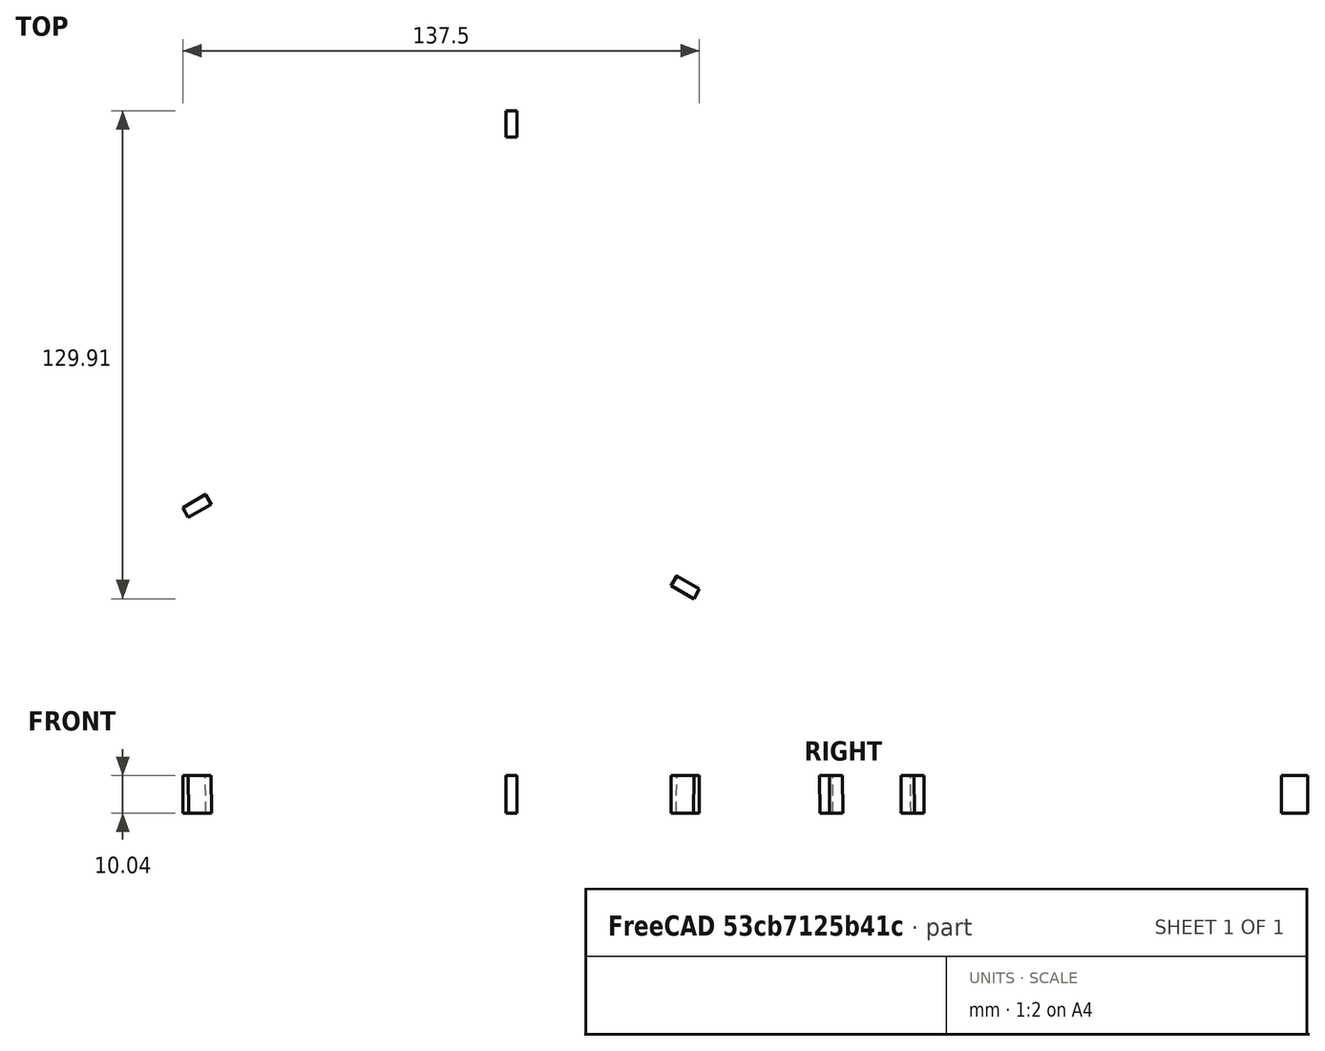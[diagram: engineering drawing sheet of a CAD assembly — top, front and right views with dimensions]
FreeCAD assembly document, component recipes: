
FREECAD ASSEMBLY — COMPONENT RECIPES ("deltarobot-example")

This assembly document has 17 components, labeled P0..P16 below (a component is one placed body or linked part). 17 of them carry a construction recipe — the FreeCAD feature program that regenerates the part from scratch, quoted from this document or its linked companion documents; the rest are supplied as boundary geometry only. No exploded tour is included for this assembly.
COMPONENT P0 — recipe-attached ("arm", a linked part whose construction recipe lives in a companion FreeCAD document of the same project; that document's serialized recipe follows).
Construction recipe (the companion document, serialized — sketch geometry with constraints, then the solid features built on it; lengths are millimeters unless a unit is written):

FCSTD DOCUMENT  (FreeCAD 2024.1R35694 (Git))
Label: arm
License: All rights reserved
LicenseURL: http://en.wikipedia.org/wiki/All_rights_reserved
objects: Sketcher::SketchObject×11, PartDesign::Pad×6, PartDesign::Plane×2, PartDesign::Revolution×2, PartDesign::Mirrored×2, PartDesign::Body×2, PartDesign::Pocket×2, PartDesign::Chamfer×1, PartDesign::Hole×1, PartDesign::Fillet×1, App::Part×1
note: 43 computed .brp shape members not serialized (recipe doc carries the construction recipe); baked Part::Feature solids carry a one-line shape summary decoded from their .brp

FEATURE [PartDesign::Plane] DatumPlane002  label="midplane001"
  AttachmentOffset = pos=(0,0,7) rot=(0,0,1;0rad)
  Length = 60
  MapMode = 5
  Placement = pos=(0,-7,1.6e-15) rot=(1,0,0;1.5708rad)
  ResizeMode = 0
  Support = -> [XZ_Plane002]
  Width = 60
FEATURE [Sketcher::SketchObject] Sketch008
  FullyConstrained = true
  MapMode = 5
  Placement = pos=(0,0,0) rot=(1,0,0;1.5708rad)
  Support = -> [XZ_Plane002]
  sketch-geometry (5):
    g0: Circle CenterX=0 CenterY=0 CenterZ=0 NormalX=0 NormalY=0 NormalZ=1 AngleXU=0 Radius=2.5
    g1: ArcOfCircle CenterX=0 CenterY=0 CenterZ=0 NormalX=0 NormalY=0 NormalZ=1 AngleXU=0 Radius=6 StartAngle=3.14159 EndAngle=6.28319
    g2: LineSegment StartX=-6 StartY=-1.9e-15 StartZ=0 EndX=-6 EndY=50 EndZ=0
    g3: LineSegment StartX=6 StartY=-1.5e-15 StartZ=0 EndX=6 EndY=50 EndZ=0
    g4: LineSegment StartX=-6 StartY=50 StartZ=0 EndX=6 EndY=50 EndZ=0
  constraints (12):
    c: Coincident(g0,g-1)
    c: Tangent(g1,g2) = 1.5708
    c: Tangent(g1,g3) = -1.5708
    c: Vertical(g3)
    c: Diameter(g0) = 5
    c: Distance(g1,g1) = 12
    c: PointOnObject(g1,g-1)
    c: Coincident(g4,g2)
    c: Coincident(g4,g3)
    c: DistanceY(g3,g3) = 50
    c: Vertical(g2)
    c: Symmetric(g2,g3,g-2)
FEATURE [PartDesign::Pad] Pad003
  Direction = (0,-1,2e-16)
  Length = 8
  Length2 = 10
  Midplane = true
  Placement = pos=(0,0,0) rot=(1,0,0;1.5708rad)
  Profile = -> Sketch008
  ReferenceAxis = -> Sketch008 [N_Axis]
  Type = 0
FEATURE [Sketcher::SketchObject] Sketch009
  FullyConstrained = true
  MapMode = 5
  Placement = pos=(0,0,0) rot=(1,0,0;1.5708rad)
  Support = -> [XZ_Plane002]
  sketch-geometry (2):
    g0: Circle CenterX=0 CenterY=0 CenterZ=0 NormalX=0 NormalY=0 NormalZ=1 AngleXU=0 Radius=2.5
    g1: Circle CenterX=0 CenterY=0 CenterZ=0 NormalX=0 NormalY=0 NormalZ=1 AngleXU=0 Radius=6
  constraints (4):
    c: Coincident(g0,g-1)
    c: Coincident(g1,g0)
    c: Diameter(g0) = 5
    c: Diameter(g1) = 12
FEATURE [PartDesign::Pad] Pad004
  BaseFeature = -> Pad003
  Direction = (0,-1,2e-16)
  Length = 10
  Length2 = 10
  Placement = pos=(0,0,0) rot=(1,0,0;1.5708rad)
  Profile = -> Sketch009
  ReferenceAxis = -> Sketch009 [N_Axis]
  Refine = true
  Type = 0
FEATURE [Sketcher::SketchObject] Sketch010
  ExternalGeometry = -> [Pad004]
  FullyConstrained = true
  MapMode = 5
  Placement = pos=(0,-7,1.6e-15) rot=(1,0,0;1.5708rad)
  Support = -> [DatumPlane002]
  sketch-geometry (4):
    g0: LineSegment StartX=-6 StartY=50 StartZ=0 EndX=6 EndY=50 EndZ=0
    g1: LineSegment StartX=6 StartY=50 StartZ=0 EndX=6 EndY=56 EndZ=0
    g2: LineSegment StartX=6 StartY=56 StartZ=0 EndX=-6 EndY=56 EndZ=0
    g3: LineSegment StartX=-6 StartY=56 StartZ=0 EndX=-6 EndY=50 EndZ=0
  constraints (10):
    c: Coincident(g0,g1)
    c: Coincident(g1,g2)
    c: Coincident(g2,g3)
    c: Coincident(g3,g0)
    c: Horizontal(g2)
    c: Vertical(g1)
    c: Vertical(g3)
    c: Coincident(g0,g-3)
    c: Coincident(g0,g-3)
    c: DistanceY(g1,g1) = 6
FEATURE [PartDesign::Pad] Pad005
  BaseFeature = -> Pad004
  Direction = (0,-1,2e-16)
  Length = 36
  Length2 = 10
  Midplane = true
  Placement = pos=(0,0,0) rot=(1,0,0;1.5708rad)
  Profile = -> Sketch010
  ReferenceAxis = -> Sketch010 [N_Axis]
  Refine = true
  Type = 0
FEATURE [Sketcher::SketchObject] Sketch011
  ExternalGeometry = -> [Pad005,DatumPlane002]
  FullyConstrained = true
  MapMode = 5
  Placement = pos=(0,0,0) rot=(0.57735,0.57735,0.57735;2.0944rad)
  Support = -> [YZ_Plane002]
  sketch-geometry (4):
    g0: LineSegment StartX=-37 StartY=53 StartZ=0 EndX=-25 EndY=53 EndZ=0
    g1: ArcOfCircle CenterX=-32 CenterY=53 CenterZ=0 NormalX=0 NormalY=0 NormalZ=1 AngleXU=0 Radius=5 StartAngle=0.643501 EndAngle=3.14159
    g2: LineSegment StartX=-28 StartY=56 StartZ=0 EndX=-25 EndY=56 EndZ=0
    g3: LineSegment StartX=-25 StartY=56 StartZ=0 EndX=-25 EndY=53 EndZ=0
  constraints (12):
    c: Symmetric(g-3,g-3,g0)
    c: PointOnObject(g1,g0)
    c: Coincident(g1,g0)
    c: PointOnObject(g0,g-3)
    c: Radius(g1) = 5
    c: Distance(g1,g-4) = 25
    c: Coincident(g1,g2)
    c: PointOnObject(g2,g-3)
    c: Horizontal(g2)
    c: Coincident(g2,g3)
    c: Coincident(g3,g0)
    c: DistanceY(g0,g2) = 3
FEATURE [PartDesign::Revolution] Revolution
  Angle = 360
  Angle2 = 60
  Axis = (0,1,0)
  Base = (0,-37,53)
  BaseFeature = -> Pad005
  Placement = pos=(0,0,0) rot=(1,0,0;1.5708rad)
  Profile = -> Sketch011
  ReferenceAxis = -> Sketch011 [Edge1]
  Refine = true
  Type = 0
FEATURE [PartDesign::Mirrored] Mirrored002
  BaseFeature = -> Revolution
  MirrorPlane = -> DatumPlane002
  Originals = -> [Revolution]
  Placement = pos=(0,0,0) rot=(1,0,0;1.5708rad)
  Refine = true
FEATURE [PartDesign::Body] Body001  label="arm-skeleton"
  Group = -> [Sketch008,Pad003,Sketch009,Pad004,DatumPlane002,Sketch010,Pad005,Sketch011,Revolution,Mirrored002]
  Origin = -> Origin002
  Tip = -> Mirrored002
FEATURE [PartDesign::Plane] DatumPlane003  label="midplane002"
  AttachmentOffset = pos=(0,0,7) rot=(0,0,1;0rad)
  Length = 60
  MapMode = 5
  Placement = pos=(0,-7,1.6e-15) rot=(1,0,0;1.5708rad)
  ResizeMode = 0
  Support = -> [XZ_Plane002]
  Width = 60
FEATURE [Sketcher::SketchObject] Sketch012
  FullyConstrained = true
  MapMode = 5
  Placement = pos=(0,0,0) rot=(1,0,0;1.5708rad)
  Support = -> [XZ_Plane003]
  sketch-geometry (5):
    g0: Circle CenterX=0 CenterY=0 CenterZ=0 NormalX=0 NormalY=0 NormalZ=1 AngleXU=0 Radius=2.5
    g1: ArcOfCircle CenterX=0 CenterY=0 CenterZ=0 NormalX=0 NormalY=0 NormalZ=1 AngleXU=0 Radius=6 StartAngle=3.14159 EndAngle=6.28319
    g2: LineSegment StartX=-6 StartY=-1.9e-15 StartZ=0 EndX=-6 EndY=50 EndZ=0
    g3: LineSegment StartX=6 StartY=-1.5e-15 StartZ=0 EndX=6 EndY=50 EndZ=0
    g4: LineSegment StartX=-6 StartY=50 StartZ=0 EndX=6 EndY=50 EndZ=0
  constraints (12):
    c: Coincident(g0,g-1)
    c: Tangent(g1,g2) = 1.5708
    c: Tangent(g1,g3) = -1.5708
    c: Vertical(g3)
    c: Diameter(g0) = 5
    c: Distance(g1,g1) = 12
    c: PointOnObject(g1,g-1)
    c: Coincident(g4,g2)
    c: Coincident(g4,g3)
    c: DistanceY(g3,g3) = 50
    c: Vertical(g2)
    c: Symmetric(g2,g3,g-2)
FEATURE [PartDesign::Pad] Pad006
  Direction = (0,-1,2e-16)
  Length = 8
  Length2 = 10
  Midplane = true
  Placement = pos=(0,0,0) rot=(1,0,0;1.5708rad)
  Profile = -> Sketch012
  ReferenceAxis = -> Sketch012 [N_Axis]
  Type = 0
FEATURE [Sketcher::SketchObject] Sketch013
  FullyConstrained = true
  MapMode = 5
  Placement = pos=(0,0,0) rot=(1,0,0;1.5708rad)
  Support = -> [XZ_Plane003]
  sketch-geometry (2):
    g0: Circle CenterX=0 CenterY=0 CenterZ=0 NormalX=0 NormalY=0 NormalZ=1 AngleXU=0 Radius=2.5
    g1: Circle CenterX=0 CenterY=0 CenterZ=0 NormalX=0 NormalY=0 NormalZ=1 AngleXU=0 Radius=6
  constraints (4):
    c: Coincident(g0,g-1)
    c: Coincident(g1,g0)
    c: Diameter(g0) = 5
    c: Diameter(g1) = 12
FEATURE [PartDesign::Pad] Pad007
  BaseFeature = -> Pad006
  Direction = (0,-1,2e-16)
  Length = 10
  Length2 = 10
  Placement = pos=(0,0,0) rot=(1,0,0;1.5708rad)
  Profile = -> Sketch013
  ReferenceAxis = -> Sketch013 [N_Axis]
  Refine = true
  Type = 0
FEATURE [Sketcher::SketchObject] Sketch014
  ExternalGeometry = -> [Pad007]
  FullyConstrained = true
  MapMode = 5
  Placement = pos=(0,-7,1.6e-15) rot=(1,0,0;1.5708rad)
  Support = -> [DatumPlane003]
  sketch-geometry (4):
    g0: LineSegment StartX=-6 StartY=50 StartZ=0 EndX=6 EndY=50 EndZ=0
    g1: LineSegment StartX=6 StartY=50 StartZ=0 EndX=6 EndY=56 EndZ=0
    g2: LineSegment StartX=6 StartY=56 StartZ=0 EndX=-6 EndY=56 EndZ=0
    g3: LineSegment StartX=-6 StartY=56 StartZ=0 EndX=-6 EndY=50 EndZ=0
  constraints (10):
    c: Coincident(g0,g1)
    c: Coincident(g1,g2)
    c: Coincident(g2,g3)
    c: Coincident(g3,g0)
    c: Horizontal(g2)
    c: Vertical(g1)
    c: Vertical(g3)
    c: Coincident(g0,g-3)
    c: Coincident(g0,g-3)
    c: DistanceY(g1,g1) = 6
FEATURE [PartDesign::Pad] Pad008
  BaseFeature = -> Pad007
  Direction = (0,-1,2e-16)
  Length = 36
  Length2 = 10
  Midplane = true
  Placement = pos=(0,0,0) rot=(1,0,0;1.5708rad)
  Profile = -> Sketch014
  ReferenceAxis = -> Sketch014 [N_Axis]
  Refine = true
  Type = 0
FEATURE [Sketcher::SketchObject] Sketch015
  ExternalGeometry = -> [Pad008,DatumPlane003]
  FullyConstrained = true
  MapMode = 5
  Placement = pos=(0,0,0) rot=(0.57735,0.57735,0.57735;2.0944rad)
  Support = -> [YZ_Plane003]
  sketch-geometry (4):
    g0: LineSegment StartX=-36.9 StartY=53 StartZ=0 EndX=-25 EndY=53 EndZ=0
    g1: ArcOfCircle CenterX=-32 CenterY=53 CenterZ=0 NormalX=0 NormalY=0 NormalZ=1 AngleXU=0 Radius=4.9 StartAngle=0.658897 EndAngle=3.14159
    g2: LineSegment StartX=-28.1257 StartY=56 StartZ=0 EndX=-25 EndY=56 EndZ=0
    g3: LineSegment StartX=-25 StartY=56 StartZ=0 EndX=-25 EndY=53 EndZ=0
  constraints (12):
    c: Symmetric(g-3,g-3,g0)
    c: PointOnObject(g1,g0)
    c: Coincident(g1,g0)
    c: PointOnObject(g0,g-3)
    c: Radius(g1) = 4.9
    c: Distance(g1,g-4) = 25
    c: Coincident(g1,g2)
    c: PointOnObject(g2,g-3)
    c: Horizontal(g2)
    c: Coincident(g2,g3)
    c: Coincident(g3,g0)
    c: DistanceY(g0,g2) = 3
FEATURE [PartDesign::Revolution] Revolution001
  Angle = 360
  Angle2 = 60
  Axis = (0,1,0)
  Base = (0,-36.9,53)
  BaseFeature = -> Pad008
  Placement = pos=(0,0,0) rot=(1,0,0;1.5708rad)
  Profile = -> Sketch015
  ReferenceAxis = -> Sketch015 [Edge1]
  Refine = true
  Type = 0
FEATURE [PartDesign::Mirrored] Mirrored003
  BaseFeature = -> Revolution001
  MirrorPlane = -> DatumPlane003
  Originals = -> [Revolution001]
  Placement = pos=(0,0,0) rot=(1,0,0;1.5708rad)
  Refine = true
FEATURE [PartDesign::Chamfer] Chamfer
  Angle = 45
  Base = -> Mirrored003 [Edge12,Edge10,Edge17,Edge21]
  BaseFeature = -> Mirrored003
  ChamferType = 0
  FlipDirection = false
  Placement = pos=(0,0,0) rot=(1,0,0;1.5708rad)
  Refine = true
  Size = 2
  Size2 = 1
  SupportTransform = false
  UseAllEdges = false
FEATURE [Sketcher::SketchObject] Sketch
  FullyConstrained = true
  MapMode = 5
  Placement = pos=(0,0,0) rot=(1,0,0;1.5708rad)
  Support = -> [XZ_Plane003]
  sketch-geometry (4):
    g0: LineSegment StartX=0.5 StartY=0 StartZ=0 EndX=0.5 EndY=10 EndZ=0
    g1: LineSegment StartX=0.5 StartY=10 StartZ=0 EndX=-0.5 EndY=10 EndZ=0
    g2: LineSegment StartX=-0.5 StartY=10 StartZ=0 EndX=-0.5 EndY=0 EndZ=0
    g3: LineSegment StartX=-0.5 StartY=0 StartZ=0 EndX=0.5 EndY=0 EndZ=0
  constraints (11):
    c: Coincident(g0,g1)
    c: Coincident(g1,g2)
    c: Coincident(g2,g3)
    c: Coincident(g3,g0)
    c: Vertical(g0)
    c: Vertical(g2)
    c: Horizontal(g1)
    c: Horizontal(g3)
    c: Symmetric(g2,g0,g-1)
    c: Distance(g1,g1) = 1
    c: DistanceY(g0,g0) = 10
FEATURE [PartDesign::Pocket] Pocket
  BaseFeature = -> Chamfer
  Direction = (0,1,-2e-16)
  Length = 5
  Length2 = 5
  Midplane = true
  Placement = pos=(0,0,0) rot=(1,0,0;1.5708rad)
  Profile = -> Sketch
  ReferenceAxis = -> Sketch [N_Axis]
  Refine = true
  Type = 1
FEATURE [Sketcher::SketchObject] Sketch016
  FullyConstrained = true
  MapMode = 5
  Placement = pos=(6,0,0) rot=(0.707107,0,0.707107;3.14159rad)
  Support = -> [Pocket]
  sketch-geometry (1):
    g0: Circle CenterX=5 CenterY=0 CenterZ=0 NormalX=0 NormalY=0 NormalZ=1 AngleXU=0 Radius=1.5
  constraints (3):
    c: PointOnObject(g0,g-1)
    c: Diameter(g0) = 3
    c: DistanceX(g-1,g0) = 5
FEATURE [PartDesign::Hole] Hole
  BaseFeature = -> Pocket
  CustomThreadClearance = 0
  Depth = 178.805
  DepthType = 1
  Diameter = 3.4
  DrillForDepth = false
  DrillPoint = 1
  DrillPointAngle = 118
  HoleCutCountersinkAngle = 90
  HoleCutCustomValues = false
  HoleCutDepth = 0
  HoleCutDiameter = 6.1
  HoleCutType = 0
  ModelThread = false
  Placement = pos=(0,0,0) rot=(1,0,0;1.5708rad)
  Profile = -> Sketch016
  Refine = true
  Tapered = false
  TaperedAngle = 90
  ThreadClass = 0
  ThreadDepth = 178.805
  ThreadDepthType = 0
  ThreadDirection = 0
  ThreadFit = 0
  ThreadSize = 9
  ThreadType = 1
  Threaded = false
  UseCustomThreadClearance = false
FEATURE [Sketcher::SketchObject] Sketch017
  ExternalGeometry = -> [Hole]
  FullyConstrained = true
  MapMode = 5
  Placement = pos=(-6,0,0) rot=(0.707107,0,-0.707107;3.14159rad)
  Support = -> [Hole]
  sketch-geometry (7):
    g0: LineSegment StartX=-1.5359 StartY=-4e-16 StartZ=0 EndX=-3.26795 EndY=3 EndZ=0
    g1: LineSegment StartX=-3.26795 StartY=3 StartZ=0 EndX=-6.73205 EndY=3 EndZ=0
    g2: LineSegment StartX=-6.73205 StartY=3 StartZ=0 EndX=-8.4641 EndY=-9e-16 EndZ=0
    g3: LineSegment StartX=-8.4641 StartY=-9e-16 StartZ=0 EndX=-6.73205 EndY=-3 EndZ=0
    g4: LineSegment StartX=-6.73205 StartY=-3 StartZ=0 EndX=-3.26795 EndY=-3 EndZ=0
    g5: LineSegment StartX=-3.26795 StartY=-3 StartZ=0 EndX=-1.5359 EndY=-4e-16 EndZ=0
    g6: Circle CenterX=-5 CenterY=-6e-16 CenterZ=0 NormalX=0 NormalY=0 NormalZ=1 AngleXU=0 Radius=3.4641
  constraints (16):
    c: Coincident(g0,g1)
    c: Coincident(g1,g2)
    c: Coincident(g2,g3)
    c: Coincident(g3,g4)
    c: Coincident(g4,g5)
    c: Coincident(g5,g0)
    c: Equal(g0, g1-g5) x5
    c: PointOnObject(g0,g6)
    c: PointOnObject(g1,g6)
    c: PointOnObject(g2,g6)
    c: PointOnObject(g3,g6)
    c: PointOnObject(g4,g6)
    c: PointOnObject(g5,g6)
    c: Coincident(g6,g-3)
    c: DistanceY(g4,g0) = 6
    c: Horizontal(g1)
FEATURE [PartDesign::Pocket] Pocket001
  BaseFeature = -> Hole
  Direction = (1,0,2e-16)
  Length = 3
  Length2 = 5
  Placement = pos=(0,0,0) rot=(1,0,0;1.5708rad)
  Profile = -> Sketch017
  ReferenceAxis = -> Sketch017 [N_Axis]
  Refine = true
  Type = 0
FEATURE [PartDesign::Fillet] Fillet
  Base = -> Pocket001 [Edge3,Edge46]
  BaseFeature = -> Pocket001
  Placement = pos=(0,0,0) rot=(1,0,0;1.5708rad)
  Radius = 2
  Refine = true
  SupportTransform = false
  UseAllEdges = false
FEATURE [PartDesign::Body] Body002  label="arm0"
  Group = -> [Sketch012,Pad006,Sketch013,Pad007,DatumPlane003,Sketch014,Pad008,Sketch015,Revolution001,Mirrored003,Chamfer,Sketch,Pocket,Sketch016,Hole,Sketch017,Pocket001,Fillet]
  Origin = -> Origin003
  Tip = -> Fillet
FEATURE [App::Part] Part  label="arm"
  Group = -> [Body001,Body002]
  Origin = -> Origin
COMPONENT P1 — same part as P0; its construction recipe is shown at P0.
COMPONENT P2 — same part as P0; its construction recipe is shown at P0.
COMPONENT P3 — recipe-attached ("base 🔒", a linked part whose construction recipe lives in a companion FreeCAD document of the same project; that document's serialized recipe follows).
Construction recipe (the companion document, serialized — sketch geometry with constraints, then the solid features built on it; lengths are millimeters unless a unit is written):

FCSTD DOCUMENT  (FreeCAD 0.22R35451 (Git))
Label: base
License: All rights reserved
LicenseURL: http://en.wikipedia.org/wiki/All_rights_reserved
objects: Sketcher::SketchObject×7, PartDesign::Pad×5, PartDesign::Plane×4, PartDesign::PolarPattern×3, PartDesign::Body×2, PartDesign::Hole×1, PartDesign::Pocket×1, App::Part×1
note: 30 computed .brp shape members not serialized (recipe doc carries the construction recipe); baked Part::Feature solids carry a one-line shape summary decoded from their .brp

FEATURE [PartDesign::Plane] DatumPlane
  Length = 60
  MapMode = 5
  Placement = pos=(0,0,0) rot=(0.57735,0.57735,0.57735;2.0944rad)
  ResizeMode = 0
  Support = -> [YZ_Plane002]
  Width = 60
FEATURE [Sketcher::SketchObject] Sketch001
  FullyConstrained = true
  MapMode = 5
  Placement = pos=(0,0,0) rot=(0.57735,0.57735,0.57735;2.0944rad)
  Support = -> [DatumPlane]
  sketch-geometry (5):
    g0: Circle CenterX=75 CenterY=0 CenterZ=0 NormalX=0 NormalY=0 NormalZ=1 AngleXU=0 Radius=11.25
    g1: LineSegment StartX=96 StartY=21 StartZ=0 EndX=0 EndY=21 EndZ=0
    g2: LineSegment StartX=0 StartY=21 StartZ=0 EndX=0 EndY=-26 EndZ=0
    g3: LineSegment StartX=0 StartY=-26 StartZ=0 EndX=96 EndY=-26 EndZ=0
    g4: LineSegment StartX=96 StartY=-26 StartZ=0 EndX=96 EndY=21 EndZ=0
  constraints (15):
    c: PointOnObject(g0,g-1)
    c: Diameter(g0) = 22.5
    c: DistanceX(g-1,g0) = 75
    c: Coincident(g1,g2)
    c: Coincident(g2,g3)
    c: Coincident(g3,g4)
    c: Coincident(g4,g1)
    c: Horizontal(g1)
    c: Horizontal(g3)
    c: Vertical(g2)
    c: PointOnObject(g2,g-2)
    c: DistanceX(g0,g1) = 21
    c: DistanceY(g-1,g1) = 21
    c: DistanceY(g3,g-1) = 26
    c: Vertical(g4)
FEATURE [PartDesign::Pad] Pad001
  Direction = (1,0,0)
  Length = 5
  Length2 = 10
  Placement = pos=(0,0,0) rot=(0.57735,0.57735,0.57735;2.0944rad)
  Profile = -> Sketch001
  ReferenceAxis = -> Sketch001 [N_Axis]
  Reversed = true
  Type = 0
FEATURE [Sketcher::SketchObject] Sketch002
  ExternalGeometry = -> [Pad001]
  FullyConstrained = true
  MapMode = 5
  Placement = pos=(0,0,0) rot=(0.57735,0.57735,0.57735;2.0944rad)
  Support = -> [Pad001]
  sketch-geometry (5):
    g0: Circle CenterX=90.5 CenterY=15.5 CenterZ=0 NormalX=0 NormalY=0 NormalZ=1 AngleXU=0 Radius=2
    g1: LineSegment StartX=75 StartY=0 StartZ=0 EndX=75 EndY=11.25 EndZ=0
    g2: Circle CenterX=90.5 CenterY=-15.5 CenterZ=0 NormalX=0 NormalY=0 NormalZ=1 AngleXU=0 Radius=2
    g3: Circle CenterX=59.5 CenterY=-15.5 CenterZ=0 NormalX=0 NormalY=0 NormalZ=1 AngleXU=0 Radius=2
    g4: Circle CenterX=59.5 CenterY=15.5 CenterZ=0 NormalX=0 NormalY=0 NormalZ=1 AngleXU=0 Radius=2
  constraints (12):
    c: Coincident(g1,g-3)
    c: PointOnObject(g1,g-3)
    c: Vertical(g1)
    c: Symmetric(g0,g4,g1)
    c: Symmetric(g0,g2,g-1)
    c: Symmetric(g2,g3,g1)
    c: Equal(g4,g0)
    c: Equal(g0,g2)
    c: Equal(g2,g3)
    c: DistanceX(g4,g0) = 31
    c: DistanceY(g2,g0) = 31
    c: Diameter(g0) = 4
FEATURE [PartDesign::Hole] Hole
  BaseFeature = -> Pad001
  CustomThreadClearance = 0
  Depth = 25
  DepthType = 0
  Diameter = 3.4
  DrillForDepth = false
  DrillPoint = 1
  DrillPointAngle = 118
  HoleCutCountersinkAngle = 90
  HoleCutCustomValues = false
  HoleCutDepth = 3.4
  HoleCutDiameter = 6.1
  HoleCutType = 1
  ModelThread = false
  Placement = pos=(0,0,0) rot=(0.57735,0.57735,0.57735;2.0944rad)
  Profile = -> Sketch002
  Tapered = false
  TaperedAngle = 90
  ThreadClass = 0
  ThreadDepth = 25
  ThreadDepthType = 0
  ThreadDirection = 0
  ThreadFit = 0
  ThreadSize = 9
  ThreadType = 1
  Threaded = false
  UseCustomThreadClearance = false
FEATURE [PartDesign::Plane] DatumPlane001
  Length = 60
  MapMode = 5
  Placement = pos=(2.9e-15,0,-26) rot=(0.707107,0.707107,0;3.14159rad)
  ResizeMode = 0
  Support = -> [Pad001]
  Width = 60
FEATURE [Sketcher::SketchObject] Sketch003
  FullyConstrained = true
  MapMode = 5
  Placement = pos=(2.9e-15,0,-26) rot=(0.707107,0.707107,0;3.14159rad)
  Support = -> [DatumPlane001]
  sketch-geometry (1):
    g0: Circle CenterX=0 CenterY=0 CenterZ=0 NormalX=0 NormalY=0 NormalZ=1 AngleXU=0 Radius=5
  constraints (2):
    c: Coincident(g0,g-1)
    c: Diameter(g0) = 10
FEATURE [PartDesign::Pad] Pad002
  BaseFeature = -> Hole
  Direction = (0,0,-1)
  Length = 42
  Length2 = 10
  Placement = pos=(0,0,0) rot=(0.57735,0.57735,0.57735;2.0944rad)
  Profile = -> Sketch003
  ReferenceAxis = -> Sketch003 [N_Axis]
  Refine = true
  Reversed = true
  Type = 1
FEATURE [PartDesign::PolarPattern] PolarPattern
  Angle = 360
  Axis = -> Z_Axis002
  BaseFeature = -> Pad002
  Mode = 0
  Occurrences = 3
  Offset = 120
  Originals = -> [Pad001,Hole]
  Placement = pos=(0,0,0) rot=(0.57735,0.57735,0.57735;2.0944rad)
  Refine = true
FEATURE [Sketcher::SketchObject] Sketch
  FullyConstrained = true
  MapMode = 5
  Placement = pos=(2.9e-15,0,-26) rot=(0.707107,0.707107,0;3.14159rad)
  Support = -> [DatumPlane001]
  sketch-geometry (8):
    g0: LineSegment StartX=96 StartY=0 StartZ=0 EndX=-48 EndY=83.1384 EndZ=0
    g1: LineSegment StartX=-48 StartY=83.1384 StartZ=0 EndX=-48 EndY=-83.1384 EndZ=0
    g2: LineSegment StartX=-48 StartY=-83.1384 StartZ=0 EndX=96 EndY=0 EndZ=0
    g3: Circle CenterX=0 CenterY=0 CenterZ=0 NormalX=0 NormalY=0 NormalZ=1 AngleXU=0 Radius=96
    g4: LineSegment StartX=60 StartY=0 StartZ=0 EndX=-30 EndY=51.9615 EndZ=0
    g5: LineSegment StartX=-30 StartY=51.9615 StartZ=0 EndX=-30 EndY=-51.9615 EndZ=0
    g6: LineSegment StartX=-30 StartY=-51.9615 StartZ=0 EndX=60 EndY=0 EndZ=0
    g7: Circle CenterX=0 CenterY=0 CenterZ=0 NormalX=0 NormalY=0 NormalZ=1 AngleXU=0 Radius=60
  constraints (22):
    c: Coincident(g0,g1)
    c: Coincident(g1,g2)
    c: Coincident(g2,g0)
    c: Equal(g0,g1)
    c: Equal(g0,g2)
    c: PointOnObject(g0,g3)
    c: PointOnObject(g1,g3)
    c: PointOnObject(g2,g3)
    c: Coincident(g3,g-1)
    c: PointOnObject(g2,g-1)
    c: Coincident(g4,g5)
    c: Coincident(g5,g6)
    c: Coincident(g6,g4)
    c: Equal(g4,g5)
    c: Equal(g4,g6)
    c: PointOnObject(g4,g7)
    c: PointOnObject(g5,g7)
    c: PointOnObject(g6,g7)
    c: Coincident(g7,g3)
    c: PointOnObject(g6,g-1)
    c: DistanceX(g-1,g0) = 96
    c: DistanceX(g-1,g4) = 60
FEATURE [PartDesign::Pad] Pad
  BaseFeature = -> PolarPattern
  Direction = (0,0,-1)
  Length = 4
  Length2 = 10
  Placement = pos=(0,0,0) rot=(0.57735,0.57735,0.57735;2.0944rad)
  Profile = -> Sketch
  ReferenceAxis = -> Sketch [N_Axis]
  Refine = true
  Reversed = true
  Type = 0
FEATURE [Sketcher::SketchObject] Sketch004
  ExternalGeometry = -> [Pad]
  FullyConstrained = true
  MapMode = 5
  Placement = pos=(0,0,0) rot=(0.57735,0.57735,0.57735;2.0944rad)
  Support = -> [YZ_Plane002]
  sketch-geometry (4):
    g0: LineSegment StartX=82 StartY=21 StartZ=0 EndX=68 EndY=21 EndZ=0
    g1: LineSegment StartX=68 StartY=21 StartZ=0 EndX=68 EndY=8.80696 EndZ=0
    g2: LineSegment StartX=68 StartY=8.80696 StartZ=0 EndX=82 EndY=8.80696 EndZ=0
    g3: LineSegment StartX=82 StartY=8.80696 StartZ=0 EndX=82 EndY=21 EndZ=0
  constraints (12):
    c: Coincident(g0,g1)
    c: Coincident(g1,g2)
    c: Coincident(g2,g3)
    c: Coincident(g3,g0)
    c: Horizontal(g0)
    c: Horizontal(g2)
    c: Vertical(g1)
    c: Vertical(g3)
    c: PointOnObject(g0,g-4)
    c: PointOnObject(g1,g-3)
    c: PointOnObject(g2,g-3)
    c: DistanceX(g0,g0) = 14
FEATURE [PartDesign::Pocket] Pocket
  BaseFeature = -> Pad
  Direction = (-1,0,0)
  Length = 5
  Length2 = 5
  Placement = pos=(0,0,0) rot=(0.57735,0.57735,0.57735;2.0944rad)
  Profile = -> Sketch004
  ReferenceAxis = -> Sketch004 [N_Axis]
  Refine = true
  Type = 0
FEATURE [PartDesign::PolarPattern] PolarPattern001
  Angle = 360
  Axis = -> Z_Axis002
  BaseFeature = -> Pocket
  Mode = 0
  Occurrences = 3
  Offset = 120
  Originals = -> [Pocket]
  Placement = pos=(0,0,0) rot=(0.57735,0.57735,0.57735;2.0944rad)
  Refine = true
FEATURE [PartDesign::Body] Body001  label="base0"
  Group = -> [DatumPlane,Sketch001,Pad001,DatumPlane001,Sketch002,Hole,Sketch003,Pad002,PolarPattern,Sketch,Pad,Sketch004,Pocket,PolarPattern001]
  Origin = -> Origin002
  Tip = -> PolarPattern001
FEATURE [PartDesign::Plane] DatumPlane002
  Length = 60
  MapMode = 5
  Placement = pos=(0,0,0) rot=(0.57735,0.57735,0.57735;2.0944rad)
  ResizeMode = 0
  Support = -> [YZ_Plane003]
  Width = 60
FEATURE [Sketcher::SketchObject] Sketch006
  FullyConstrained = true
  MapMode = 5
  Placement = pos=(0,0,0) rot=(0.57735,0.57735,0.57735;2.0944rad)
  Support = -> [DatumPlane002]
  sketch-geometry (5):
    g0: Circle CenterX=75 CenterY=0 CenterZ=0 NormalX=0 NormalY=0 NormalZ=1 AngleXU=0 Radius=11.25
    g1: LineSegment StartX=96 StartY=21 StartZ=0 EndX=0 EndY=21 EndZ=0
    g2: LineSegment StartX=0 StartY=21 StartZ=0 EndX=0 EndY=-26 EndZ=0
    g3: LineSegment StartX=0 StartY=-26 StartZ=0 EndX=96 EndY=-26 EndZ=0
    g4: LineSegment StartX=96 StartY=-26 StartZ=0 EndX=96 EndY=21 EndZ=0
  constraints (15):
    c: PointOnObject(g0,g-1)
    c: Diameter(g0) = 22.5
    c: DistanceX(g-1,g0) = 75
    c: Coincident(g1,g2)
    c: Coincident(g2,g3)
    c: Coincident(g3,g4)
    c: Coincident(g4,g1)
    c: Horizontal(g1)
    c: Horizontal(g3)
    c: Vertical(g2)
    c: PointOnObject(g2,g-2)
    c: DistanceX(g0,g1) = 21
    c: DistanceY(g-1,g1) = 21
    c: DistanceY(g3,g-1) = 26
    c: Vertical(g4)
FEATURE [PartDesign::Pad] Pad004
  Direction = (1,0,0)
  Length = 5
  Length2 = 10
  Placement = pos=(0,0,0) rot=(0.57735,0.57735,0.57735;2.0944rad)
  Profile = -> Sketch006
  ReferenceAxis = -> Sketch006 [N_Axis]
  Reversed = true
  Type = 0
FEATURE [PartDesign::Plane] DatumPlane003
  Length = 60
  MapMode = 5
  Placement = pos=(2.9e-15,0,-26) rot=(0.707107,0.707107,0;3.14159rad)
  ResizeMode = 0
  Support = -> [Pad004]
  Width = 60
FEATURE [Sketcher::SketchObject] Sketch008
  FullyConstrained = true
  MapMode = 5
  Placement = pos=(2.9e-15,0,-26) rot=(0.707107,0.707107,0;3.14159rad)
  Support = -> [DatumPlane003]
  sketch-geometry (1):
    g0: Circle CenterX=0 CenterY=0 CenterZ=0 NormalX=0 NormalY=0 NormalZ=1 AngleXU=0 Radius=5
  constraints (2):
    c: Coincident(g0,g-1)
    c: Diameter(g0) = 10
FEATURE [PartDesign::Pad] Pad005
  BaseFeature = -> Pad004
  Direction = (0,0,-1)
  Length = 42
  Length2 = 10
  Placement = pos=(0,0,0) rot=(0.57735,0.57735,0.57735;2.0944rad)
  Profile = -> Sketch008
  ReferenceAxis = -> Sketch008 [N_Axis]
  Refine = true
  Reversed = true
  Type = 1
FEATURE [PartDesign::PolarPattern] PolarPattern002
  Angle = 360
  Axis = -> Z_Axis003
  BaseFeature = -> Pad005
  Mode = 0
  Occurrences = 3
  Offset = 120
  Originals = -> [Pad004]
  Placement = pos=(0,0,0) rot=(0.57735,0.57735,0.57735;2.0944rad)
  Refine = true
FEATURE [PartDesign::Body] Body002  label="base-skeleton"
  Group = -> [DatumPlane002,Sketch006,Pad004,DatumPlane003,Sketch008,Pad005,PolarPattern002]
  Origin = -> Origin003
  Tip = -> PolarPattern002
FEATURE [App::Part] Part  label="base"
  Group = -> [Body002,Body001]
  Origin = -> Origin
COMPONENT P4 — recipe-attached ("cone", a linked part whose construction recipe lives in a companion FreeCAD document of the same project; that document's serialized recipe follows).
Construction recipe (the companion document, serialized — sketch geometry with constraints, then the solid features built on it; lengths are millimeters unless a unit is written):

FCSTD DOCUMENT  (FreeCAD 0.22R35451 (Git))
Label: cone
License: All rights reserved
LicenseURL: http://en.wikipedia.org/wiki/All_rights_reserved
objects: Sketcher::SketchObject×1, PartDesign::Revolution×1, PartDesign::Body×1, App::Part×1
note: 4 computed .brp shape members not serialized (recipe doc carries the construction recipe); baked Part::Feature solids carry a one-line shape summary decoded from their .brp

FEATURE [Sketcher::SketchObject] Sketch
  FullyConstrained = true
  MapMode = 5
  Placement = pos=(0,0,0) rot=(1,0,0;1.5708rad)
  Support = -> [XZ_Plane001]
  sketch-geometry (4):
    g0: LineSegment StartX=0 StartY=0 StartZ=0 EndX=0 EndY=20 EndZ=0
    g1: LineSegment StartX=0 StartY=20 StartZ=0 EndX=2 EndY=20 EndZ=0
    g2: ArcOfCircle CenterX=31 CenterY=20 CenterZ=0 NormalX=0 NormalY=0 NormalZ=1 AngleXU=0 Radius=29 StartAngle=3.14159 EndAngle=3.90261
    g3: LineSegment StartX=10 StartY=0 StartZ=0 EndX=0 EndY=0 EndZ=0
  constraints (11):
    c: Coincident(g-1,g0)
    c: PointOnObject(g0,g-2)
    c: Coincident(g0,g1)
    c: Horizontal(g1)
    c: Perpendicular(g1,g2) = 4.71239
    c: PointOnObject(g2,g-1)
    c: Coincident(g2,g3)
    c: Coincident(g3,g0)
    c: DistanceX(g1,g1) = 2
    c: DistanceX(g3,g3) = 10
    c: DistanceY(g0,g0) = 20
FEATURE [PartDesign::Revolution] Revolution
  Angle = 360
  Angle2 = 60
  Axis = (0,2e-16,1)
  Base = (0,0,0)
  Placement = pos=(0,0,0) rot=(1,0,0;1.5708rad)
  Profile = -> Sketch
  ReferenceAxis = -> Sketch [V_Axis]
  Refine = true
  Reversed = true
  Type = 0
FEATURE [PartDesign::Body] Body  label="cone0"
  Group = -> [Sketch,Revolution]
  Origin = -> Origin001
  Tip = -> Revolution
FEATURE [App::Part] Part  label="cone"
  Group = -> [Body]
  Origin = -> Origin
COMPONENT P5 — same part as P4; its construction recipe is shown at P4.
COMPONENT P6 — same part as P4; its construction recipe is shown at P4.
COMPONENT P7 — recipe-attached ("link", a linked part whose construction recipe lives in a companion FreeCAD document of the same project; that document's serialized recipe follows).
Construction recipe (the companion document, serialized — sketch geometry with constraints, then the solid features built on it; lengths are millimeters unless a unit is written):

FCSTD DOCUMENT  (FreeCAD 0.22R35451 (Git))
Label: link
License: All rights reserved
LicenseURL: http://en.wikipedia.org/wiki/All_rights_reserved
objects: Sketcher::SketchObject×5, PartDesign::Pad×2, PartDesign::Groove×2, PartDesign::Mirrored×2, PartDesign::Body×2, PartDesign::Pocket×1, PartDesign::Fillet×1, App::Part×1
note: 21 computed .brp shape members not serialized (recipe doc carries the construction recipe); baked Part::Feature solids carry a one-line shape summary decoded from their .brp

FEATURE [Sketcher::SketchObject] Sketch
  FullyConstrained = true
  MapMode = 5
  Support = -> [XY_Plane001]
  sketch-geometry (4):
    g0: ArcOfCircle CenterX=-70 CenterY=0 CenterZ=0 NormalX=0 NormalY=0 NormalZ=1 AngleXU=0 Radius=8 StartAngle=0.384397 EndAngle=5.89879
    g1: ArcOfCircle CenterX=70 CenterY=0 CenterZ=0 NormalX=0 NormalY=0 NormalZ=1 AngleXU=0 Radius=8 StartAngle=3.52599 EndAngle=9.04038
    g2: LineSegment StartX=-62.5838 StartY=-3 StartZ=0 EndX=62.5838 EndY=-3 EndZ=0
    g3: LineSegment StartX=62.5838 StartY=3 StartZ=0 EndX=-62.5838 EndY=3 EndZ=0
  constraints (13):
    c: PointOnObject(g0,g-1)
    c: Symmetric(g0,g1,g-1)
    c: Equal(g0,g1)
    c: DistanceX(g0,g1) = 140
    c: Horizontal(g2)
    c: Horizontal(g3)
    c: Coincident(g0,g3)
    c: Coincident(g1,g2)
    c: Coincident(g2,g0)
    c: Vertical(g0,g0)
    c: Radius(g0) = 8
    c: Distance(g0,g0) = 6
    c: Coincident(g1,g3)
FEATURE [PartDesign::Pad] Pad
  Direction = (0,0,1)
  Length = 6
  Length2 = 4
  Midplane = true
  Profile = -> Sketch
  ReferenceAxis = -> Sketch [N_Axis]
  Refine = true
  Type = 4
FEATURE [Sketcher::SketchObject] Sketch001
  FullyConstrained = true
  MapMode = 5
  Placement = pos=(0,0,0) rot=(1,0,0;1.5708rad)
  Support = -> [XZ_Plane001]
  sketch-geometry (4):
    g0: ArcOfCircle CenterX=-70 CenterY=0 CenterZ=0 NormalX=0 NormalY=0 NormalZ=1 AngleXU=0 Radius=5 StartAngle=1.5708 EndAngle=3.54431
    g1: LineSegment StartX=-74.6 StartY=-1.95959 StartZ=0 EndX=-79.2421 EndY=-10 EndZ=0
    g2: LineSegment StartX=-79.2421 StartY=-10 StartZ=0 EndX=-70 EndY=-10 EndZ=0
    g3: LineSegment StartX=-70 StartY=5 StartZ=0 EndX=-70 EndY=-10 EndZ=0
  constraints (13):
    c: Coincident(g1,g2)
    c: Horizontal(g2)
    c: PointOnObject(g0,g-1)
    c: Coincident(g3,g0)
    c: Coincident(g3,g2)
    c: Vertical(g3)
    c: PointOnObject(g0,g3)
    c: Radius(g0) = 5
    c: DistanceX(g0,g2) = 4.6
    c: DistanceX(g0,g-1) = 70
    c: Angle(g1,g3) = 0.523599
    c: DistanceY(g3,g3) = 15
    c: Coincident(g1,g0)
FEATURE [PartDesign::Groove] Groove
  Angle = 360
  Angle2 = 60
  Axis = (0,-2e-16,-1)
  Base = (-70,1.1e-15,5)
  BaseFeature = -> Pad
  Profile = -> Sketch001
  ReferenceAxis = -> Sketch001 [Edge4]
  Refine = true
  Reversed = true
  Type = 0
FEATURE [Sketcher::SketchObject] Sketch003
  FullyConstrained = true
  MapMode = 5
  Support = -> [XY_Plane002]
  sketch-geometry (4):
    g0: ArcOfCircle CenterX=-70 CenterY=0 CenterZ=0 NormalX=0 NormalY=0 NormalZ=1 AngleXU=0 Radius=8 StartAngle=0.384397 EndAngle=5.89879
    g1: ArcOfCircle CenterX=70 CenterY=0 CenterZ=0 NormalX=0 NormalY=0 NormalZ=1 AngleXU=0 Radius=8 StartAngle=3.52599 EndAngle=9.04038
    g2: LineSegment StartX=-62.5838 StartY=-3 StartZ=0 EndX=62.5838 EndY=-3 EndZ=0
    g3: LineSegment StartX=62.5838 StartY=3 StartZ=0 EndX=-62.5838 EndY=3 EndZ=0
  constraints (13):
    c: PointOnObject(g0,g-1)
    c: Symmetric(g0,g1,g-1)
    c: Equal(g0,g1)
    c: DistanceX(g0,g1) = 140
    c: Horizontal(g2)
    c: Horizontal(g3)
    c: Coincident(g0,g3)
    c: Coincident(g1,g2)
    c: Coincident(g2,g0)
    c: Vertical(g0,g0)
    c: Radius(g0) = 8
    c: Distance(g0,g0) = 6
    c: Coincident(g1,g3)
FEATURE [PartDesign::Pad] Pad001
  Direction = (0,0,1)
  Length = 6
  Length2 = 4
  Midplane = true
  Profile = -> Sketch003
  ReferenceAxis = -> Sketch003 [N_Axis]
  Refine = true
  Type = 4
FEATURE [Sketcher::SketchObject] Sketch004
  FullyConstrained = true
  MapMode = 5
  Placement = pos=(0,0,0) rot=(1,0,0;1.5708rad)
  Support = -> [XZ_Plane001]
  sketch-geometry (4):
    g0: ArcOfCircle CenterX=-70 CenterY=0 CenterZ=0 NormalX=0 NormalY=0 NormalZ=1 AngleXU=0 Radius=5 StartAngle=1.5708 EndAngle=3.54431
    g1: LineSegment StartX=-74.6 StartY=-1.95959 StartZ=0 EndX=-79.2421 EndY=-10 EndZ=0
    g2: LineSegment StartX=-79.2421 StartY=-10 StartZ=0 EndX=-70 EndY=-10 EndZ=0
    g3: LineSegment StartX=-70 StartY=5 StartZ=0 EndX=-70 EndY=-10 EndZ=0
  constraints (13):
    c: Coincident(g1,g2)
    c: Horizontal(g2)
    c: PointOnObject(g0,g-1)
    c: Coincident(g3,g0)
    c: Coincident(g3,g2)
    c: Vertical(g3)
    c: PointOnObject(g0,g3)
    c: Radius(g0) = 5
    c: DistanceX(g0,g2) = 4.6
    c: DistanceX(g0,g-1) = 70
    c: Angle(g1,g3) = 0.523599
    c: DistanceY(g3,g3) = 15
    c: Coincident(g1,g0)
FEATURE [PartDesign::Groove] Groove001
  Angle = 360
  Angle2 = 60
  Axis = (0,-2e-16,-1)
  Base = (-70,1.1e-15,5)
  BaseFeature = -> Pad001
  Profile = -> Sketch004
  ReferenceAxis = -> Sketch004 [Edge4]
  Refine = true
  Reversed = true
  Type = 0
FEATURE [Sketcher::SketchObject] Sketch005
  ExternalGeometry = -> [Sketch004]
  FullyConstrained = true
  MapMode = 5
  Placement = pos=(0,0,-4) rot=(1,0,0;3.14159rad)
  Support = -> [Groove001]
  sketch-geometry (4):
    g0: LineSegment StartX=-71 StartY=0.5 StartZ=0 EndX=-81 EndY=0.5 EndZ=0
    g1: LineSegment StartX=-81 StartY=0.5 StartZ=0 EndX=-81 EndY=-0.5 EndZ=0
    g2: LineSegment StartX=-81 StartY=-0.5 StartZ=0 EndX=-71 EndY=-0.5 EndZ=0
    g3: LineSegment StartX=-71 StartY=-0.5 StartZ=0 EndX=-71 EndY=0.5 EndZ=0
  constraints (11):
    c: Coincident(g0,g1)
    c: Coincident(g1,g2)
    c: Coincident(g2,g3)
    c: Coincident(g3,g0)
    c: Horizontal(g0)
    c: Horizontal(g2)
    c: Vertical(g1)
    c: Symmetric(g2,g0,g-1)
    c: Distance(g3,g3) = 1
    c: DistanceX(g2,g-3) = 1
    c: DistanceX(g2,g2) = 10
FEATURE [PartDesign::Pocket] Pocket
  BaseFeature = -> Groove001
  Direction = (0,0,1)
  Length = 8
  Length2 = 5
  Profile = -> Sketch005
  ReferenceAxis = -> Sketch005 [N_Axis]
  Refine = true
  Type = 0
FEATURE [PartDesign::Mirrored] Mirrored
  BaseFeature = -> Groove
  MirrorPlane = -> Sketch001 [V_Axis]
  Originals = -> [Groove]
  Refine = true
FEATURE [PartDesign::Body] Body  label="link-skel"
  Group = -> [Sketch,Pad,Sketch001,Groove,Mirrored]
  Origin = -> Origin001
  Tip = -> Mirrored
FEATURE [PartDesign::Mirrored] Mirrored001
  BaseFeature = -> Pocket
  MirrorPlane = -> Sketch005 [V_Axis]
  Originals = -> [Pocket,Groove001]
  Refine = true
FEATURE [PartDesign::Fillet] Fillet
  Base = -> Mirrored001 [Edge6,Edge8,Edge31,Edge27]
  BaseFeature = -> Mirrored001
  Radius = 10
  Refine = true
  SupportTransform = false
  UseAllEdges = false
FEATURE [PartDesign::Body] Body001  label="link0"
  Group = -> [Sketch003,Pad001,Sketch004,Groove001,Sketch005,Pocket,Mirrored001,Fillet]
  Origin = -> Origin002
  Tip = -> Fillet
FEATURE [App::Part] Part  label="link"
  Group = -> [Body,Body001]
  Origin = -> Origin
COMPONENT P8 — same part as P7; its construction recipe is shown at P7.
COMPONENT P9 — same part as P7; its construction recipe is shown at P7.
COMPONENT P10 — same part as P7; its construction recipe is shown at P7.
COMPONENT P11 — same part as P7; its construction recipe is shown at P7.
COMPONENT P12 — same part as P7; its construction recipe is shown at P7.
COMPONENT P13 — recipe-attached ("nema17_049", a linked part whose construction recipe lives in a companion FreeCAD document of the same project; that document's serialized recipe follows).
Construction recipe (the companion document, serialized — sketch geometry with constraints, then the solid features built on it; lengths are millimeters unless a unit is written):

FCSTD DOCUMENT  (FreeCAD 0.22R35451 (Git))
Label: nema17-48
License: All rights reserved
LicenseURL: http://en.wikipedia.org/wiki/All_rights_reserved
objects: Sketcher::SketchObject×4, PartDesign::Pad×3, PartDesign::Chamfer×2, PartDesign::Hole×1, PartDesign::Body×1, App::Part×1
note: 17 computed .brp shape members not serialized (recipe doc carries the construction recipe); baked Part::Feature solids carry a one-line shape summary decoded from their .brp

FEATURE [Sketcher::SketchObject] Sketch
  FullyConstrained = false
  MapMode = 5
  Support = -> [XY_Plane]
  sketch-geometry (5):
    g0: LineSegment StartX=21.15 StartY=21.15 StartZ=0 EndX=-21.15 EndY=21.15 EndZ=0
    g1: LineSegment StartX=-21.15 StartY=21.15 StartZ=0 EndX=-21.15 EndY=-21.15 EndZ=0
    g2: LineSegment StartX=-21.15 StartY=-21.15 StartZ=0 EndX=21.15 EndY=-21.15 EndZ=0
    g3: LineSegment StartX=21.15 StartY=-21.15 StartZ=0 EndX=21.15 EndY=21.15 EndZ=0
    g4: Circle CenterX=0 CenterY=0 CenterZ=0 NormalX=0 NormalY=0 NormalZ=1 AngleXU=0 Radius=29.9106
  constraints (14):
    c: Coincident(g0,g1)
    c: Coincident(g1,g2)
    c: Coincident(g2,g3)
    c: Coincident(g3,g0)
    c: Equal(g0,g1)
    c: Equal(g0,g2)
    c: Equal(g0,g3)
    c: PointOnObject(g0,g4)
    c: PointOnObject(g1,g4)
    c: PointOnObject(g2,g4)
    c: PointOnObject(g3,g4)
    c: Coincident(g4,g-1)
    c: Horizontal(g0)
    c: DistanceY(g3,g3) = 42.3
FEATURE [PartDesign::Pad] Pad
  Direction = (0,0,1)
  Length = 48
  Length2 = 100
  Profile = -> Sketch
  ReferenceAxis = -> Sketch [N_Axis]
  Type = 0
FEATURE [Sketcher::SketchObject] Sketch001
  FullyConstrained = true
  MapMode = 5
  Placement = pos=(0,0,48) rot=(0,0,1;0rad)
  Support = -> [Pad]
  sketch-geometry (1):
    g0: Circle CenterX=0 CenterY=0 CenterZ=0 NormalX=0 NormalY=0 NormalZ=1 AngleXU=0 Radius=11
  constraints (2):
    c: Coincident(g0,g-1)
    c: Diameter(g0) = 22
FEATURE [PartDesign::Pad] Pad001
  BaseFeature = -> Pad
  Direction = (0,0,1)
  Length = 2
  Length2 = 100
  Profile = -> Sketch001
  ReferenceAxis = -> Sketch001 [N_Axis]
  Type = 0
FEATURE [Sketcher::SketchObject] Sketch002
  FullyConstrained = true
  MapMode = 5
  Placement = pos=(0,0,48) rot=(0,0,1;0rad)
  Support = -> [Pad001]
  sketch-geometry (1):
    g0: Circle CenterX=0 CenterY=0 CenterZ=0 NormalX=0 NormalY=0 NormalZ=1 AngleXU=0 Radius=2.5
  constraints (2):
    c: Coincident(g0,g-1)
    c: Diameter(g0) = 5
FEATURE [PartDesign::Pad] Pad002
  BaseFeature = -> Pad001
  Direction = (0,0,1)
  Length = 24
  Length2 = 100
  Profile = -> Sketch002
  ReferenceAxis = -> Sketch002 [N_Axis]
  Type = 0
FEATURE [PartDesign::Chamfer] Chamfer
  Angle = 45
  Base = -> Pad002 [Edge18]
  BaseFeature = -> Pad002
  ChamferType = 0
  FlipDirection = false
  Size = 0.5
  Size2 = 1
  SupportTransform = true
  UseAllEdges = false
FEATURE [Sketcher::SketchObject] Sketch004
  FullyConstrained = true
  MapMode = 5
  Placement = pos=(0,0,48) rot=(0,0,1;0rad)
  sketch-geometry (4):
    g0: Circle CenterX=15.5 CenterY=-15.5 CenterZ=0 NormalX=0 NormalY=0 NormalZ=1 AngleXU=0 Radius=1.25
    g1: Circle CenterX=15.5 CenterY=15.5 CenterZ=0 NormalX=0 NormalY=0 NormalZ=1 AngleXU=0 Radius=1.25
    g2: Circle CenterX=-15.5 CenterY=15.5 CenterZ=0 NormalX=0 NormalY=0 NormalZ=1 AngleXU=0 Radius=1.25
    g3: Circle CenterX=-15.5 CenterY=-15.5 CenterZ=0 NormalX=0 NormalY=0 NormalZ=1 AngleXU=0 Radius=1.25
  constraints (9):
    c: Diameter(g0) = 2.5
    c: Symmetric(g1,g0,g-1)
    c: Symmetric(g1,g2,g-2)
    c: Symmetric(g3,g2,g-1)
    c: Equal(g2,g1)
    c: Equal(g1,g3)
    c: Equal(g3,g0)
    c: DistanceX(g2,g1) = 31
    c: DistanceY(g0,g1) = 31
FEATURE [PartDesign::Hole] Hole
  BaseFeature = -> Chamfer
  CustomThreadClearance = 0
  Depth = 4
  DepthType = 0
  Diameter = 3.4
  DrillForDepth = false
  DrillPoint = 1
  DrillPointAngle = 118
  HoleCutCountersinkAngle = 90
  HoleCutCustomValues = false
  HoleCutDepth = 0
  HoleCutDiameter = 1.6
  HoleCutType = 0
  ModelThread = false
  Profile = -> Sketch004
  Tapered = false
  TaperedAngle = 90
  ThreadClass = 0
  ThreadDepth = 4
  ThreadDepthType = 0
  ThreadDirection = 0
  ThreadFit = 0
  ThreadSize = 9
  ThreadType = 1
  Threaded = false
  UseCustomThreadClearance = false
FEATURE [PartDesign::Chamfer] Chamfer001
  Angle = 45
  Base = -> Hole [Edge20,Edge17,Edge22,Edge18]
  BaseFeature = -> Hole
  ChamferType = 0
  FlipDirection = false
  Size = 5
  Size2 = 1
  SupportTransform = true
  UseAllEdges = false
FEATURE [PartDesign::Body] Body  label="nema17"
  Group = -> [Sketch,Pad,Sketch001,Pad001,Sketch002,Pad002,Chamfer,Sketch004,Hole,Chamfer001]
  Origin = -> Origin
  Placement = pos=(0,0,-50) rot=(0,0,1;0rad)
  Tip = -> Chamfer001
FEATURE [App::Part] Part  label="nema17-48"
  Group = -> [Body]
  Origin = -> Origin001
COMPONENT P14 — same part as P13; its construction recipe is shown at P13.
COMPONENT P15 — same part as P13; its construction recipe is shown at P13.
COMPONENT P16 — recipe-attached ("plate", a linked part whose construction recipe lives in a companion FreeCAD document of the same project; that document's serialized recipe follows).
Construction recipe (the companion document, serialized — sketch geometry with constraints, then the solid features built on it; lengths are millimeters unless a unit is written):

FCSTD DOCUMENT  (FreeCAD 2024.1R35694 (Git))
Label: plate
License: All rights reserved
LicenseURL: http://en.wikipedia.org/wiki/All_rights_reserved
objects: Sketcher::SketchObject×6, PartDesign::PolarPattern×3, PartDesign::Pad×2, PartDesign::Revolution×2, PartDesign::Body×2, PartDesign::Chamfer×2, PartDesign::Pocket×2, App::Part×1
note: 27 computed .brp shape members not serialized (recipe doc carries the construction recipe); baked Part::Feature solids carry a one-line shape summary decoded from their .brp

FEATURE [Sketcher::SketchObject] Sketch003
  FullyConstrained = true
  MapMode = 5
  Support = -> [XY_Plane002]
  sketch-geometry (4):
    g0: LineSegment StartX=19 StartY=0 StartZ=0 EndX=19 EndY=50 EndZ=0
    g1: LineSegment StartX=19 StartY=50 StartZ=0 EndX=-19 EndY=50 EndZ=0
    g2: LineSegment StartX=-19 StartY=50 StartZ=0 EndX=-19 EndY=0 EndZ=0
    g3: LineSegment StartX=-19 StartY=0 StartZ=0 EndX=19 EndY=0 EndZ=0
  constraints (11):
    c: Coincident(g0,g1)
    c: Coincident(g1,g2)
    c: Coincident(g2,g3)
    c: Coincident(g3,g0)
    c: Vertical(g0)
    c: Vertical(g2)
    c: Horizontal(g1)
    c: PointOnObject(g0,g-1)
    c: Symmetric(g2,g0,g-2)
    c: DistanceX(g3,g3) = 38
    c: DistanceY(g0,g0) = 50
FEATURE [PartDesign::Pad] Pad001
  Direction = (0,0,1)
  Length = 6
  Length2 = 10
  Profile = -> Sketch003
  ReferenceAxis = -> Sketch003 [N_Axis]
  Type = 0
FEATURE [Sketcher::SketchObject] Sketch
  ExternalGeometry = -> [Pad001]
  FullyConstrained = true
  MapMode = 5
  Support = -> [XY_Plane002]
  sketch-geometry (4):
    g0: LineSegment StartX=-30 StartY=50 StartZ=0 EndX=30 EndY=50 EndZ=0
    g1: ArcOfCircle CenterX=-25 CenterY=50 CenterZ=0 NormalX=0 NormalY=0 NormalZ=1 AngleXU=0 Radius=5 StartAngle=0.643501 EndAngle=3.14159
    g2: ArcOfCircle CenterX=25 CenterY=50 CenterZ=0 NormalX=0 NormalY=0 NormalZ=1 AngleXU=0 Radius=5 StartAngle=-9e-16 EndAngle=2.49809
    g3: LineSegment StartX=-21 StartY=53 StartZ=0 EndX=21 EndY=53 EndZ=0
  constraints (12):
    c: Symmetric(g0,g0,g-2)
    c: PointOnObject(g-3,g0)
    c: PointOnObject(g1,g0)
    c: Coincident(g1,g0)
    c: Coincident(g2,g0)
    c: Symmetric(g1,g2,g-2)
    c: DistanceX(g1,g2) = 50
    c: Radius(g1) = 5
    c: Coincident(g3,g1)
    c: Coincident(g3,g2)
    c: Horizontal(g3)
    c: DistanceY(g-3,g1) = 3
FEATURE [PartDesign::Revolution] Revolution
  Angle = 360
  Angle2 = 60
  Axis = (1,-1e-16,0)
  Base = (-30,50,0)
  BaseFeature = -> Pad001
  Profile = -> Sketch
  ReferenceAxis = -> Sketch [Edge1]
  Refine = true
  Type = 0
FEATURE [PartDesign::PolarPattern] PolarPattern
  Angle = 360
  Axis = -> Sketch003 [N_Axis]
  BaseFeature = -> Revolution
  Mode = 0
  Occurrences = 3
  Offset = 120
  Originals = -> [Pad001,Revolution]
  Refine = true
FEATURE [PartDesign::Body] Body001  label="plate-skel"
  Group = -> [Sketch003,Pad001,Sketch,Revolution,PolarPattern]
  Origin = -> Origin002
  Tip = -> PolarPattern
FEATURE [Sketcher::SketchObject] Sketch005
  FullyConstrained = true
  MapMode = 5
  Support = -> [XY_Plane003]
  sketch-geometry (4):
    g0: LineSegment StartX=15 StartY=0 StartZ=0 EndX=15 EndY=50 EndZ=0
    g1: LineSegment StartX=15 StartY=50 StartZ=0 EndX=-15 EndY=50 EndZ=0
    g2: LineSegment StartX=-15 StartY=50 StartZ=0 EndX=-15 EndY=0 EndZ=0
    g3: LineSegment StartX=-15 StartY=0 StartZ=0 EndX=15 EndY=0 EndZ=0
  constraints (11):
    c: Coincident(g0,g1)
    c: Coincident(g1,g2)
    c: Coincident(g2,g3)
    c: Coincident(g3,g0)
    c: Vertical(g0)
    c: Vertical(g2)
    c: Horizontal(g1)
    c: PointOnObject(g0,g-1)
    c: Symmetric(g2,g0,g-2)
    c: DistanceX(g3,g3) = 30
    c: DistanceY(g0,g0) = 50
FEATURE [PartDesign::Pad] Pad002
  Direction = (0,0,1)
  Length = 6
  Length2 = 10
  Profile = -> Sketch005
  ReferenceAxis = -> Sketch005 [N_Axis]
  Type = 0
FEATURE [Sketcher::SketchObject] Sketch004
  ExternalGeometry = -> [Pad002]
  FullyConstrained = true
  MapMode = 5
  Support = -> [XY_Plane003]
  sketch-geometry (4):
    g0: LineSegment StartX=-29.9 StartY=50 StartZ=0 EndX=29.9 EndY=50 EndZ=0
    g1: ArcOfCircle CenterX=-25 CenterY=50 CenterZ=0 NormalX=0 NormalY=0 NormalZ=1 AngleXU=0 Radius=4.9 StartAngle=0.658897 EndAngle=3.14159
    g2: ArcOfCircle CenterX=25 CenterY=50 CenterZ=0 NormalX=0 NormalY=0 NormalZ=1 AngleXU=0 Radius=4.9 StartAngle=4e-16 EndAngle=2.4827
    g3: LineSegment StartX=-21.1257 StartY=53 StartZ=0 EndX=21.1257 EndY=53 EndZ=0
  constraints (12):
    c: Symmetric(g0,g0,g-2)
    c: PointOnObject(g-3,g0)
    c: PointOnObject(g1,g0)
    c: Coincident(g1,g0)
    c: Coincident(g2,g0)
    c: Symmetric(g1,g2,g-2)
    c: DistanceX(g1,g2) = 50
    c: Radius(g1) = 4.9
    c: Coincident(g3,g1)
    c: Coincident(g3,g2)
    c: Horizontal(g3)
    c: DistanceY(g-3,g1) = 3
FEATURE [PartDesign::Revolution] Revolution001
  Angle = 360
  Angle2 = 60
  Axis = (1,0,0)
  Base = (-29.9,50,0)
  BaseFeature = -> Pad002
  Profile = -> Sketch004
  ReferenceAxis = -> Sketch004 [Edge1]
  Refine = true
  Type = 0
FEATURE [PartDesign::PolarPattern] PolarPattern001
  Angle = 360
  Axis = -> Sketch005 [N_Axis]
  BaseFeature = -> Revolution001
  Mode = 0
  Occurrences = 3
  Offset = 120
  Originals = -> [Pad002,Revolution001]
  Refine = true
FEATURE [PartDesign::Chamfer] Chamfer
  Angle = 45
  Base = -> PolarPattern001 [Edge17,Edge44,Edge35]
  BaseFeature = -> PolarPattern001
  ChamferType = 0
  FlipDirection = false
  Refine = true
  Size = 2.4
  Size2 = 1
  SupportTransform = false
  UseAllEdges = false
FEATURE [Sketcher::SketchObject] Sketch006
  FullyConstrained = true
  MapMode = 5
  Placement = pos=(0,0,0) rot=(1,0,0;3.14159rad)
  Support = -> [Chamfer]
  sketch-geometry (7):
    g0: LineSegment StartX=25.9808 StartY=45 StartZ=0 EndX=-25.9808 EndY=45 EndZ=0
    g1: LineSegment StartX=-25.9808 StartY=45 StartZ=0 EndX=-51.9615 EndY=0 EndZ=0
    g2: LineSegment StartX=-51.9615 StartY=0 StartZ=0 EndX=-25.9808 EndY=-45 EndZ=0
    g3: LineSegment StartX=-25.9808 StartY=-45 StartZ=0 EndX=25.9808 EndY=-45 EndZ=0
    g4: LineSegment StartX=25.9808 StartY=-45 StartZ=0 EndX=51.9615 EndY=0 EndZ=0
    g5: LineSegment StartX=51.9615 StartY=0 StartZ=0 EndX=25.9808 EndY=45 EndZ=0
    g6: Circle CenterX=0 CenterY=0 CenterZ=0 NormalX=0 NormalY=0 NormalZ=1 AngleXU=0 Radius=51.9615
  constraints (16):
    c: Coincident(g0,g1)
    c: Coincident(g1,g2)
    c: Coincident(g2,g3)
    c: Coincident(g3,g4)
    c: Coincident(g4,g5)
    c: Coincident(g5,g0)
    c: Equal(g0, g1-g5) x5
    c: PointOnObject(g0,g6)
    c: PointOnObject(g1,g6)
    c: PointOnObject(g2,g6)
    c: PointOnObject(g3,g6)
    c: PointOnObject(g4,g6)
    c: PointOnObject(g5,g6)
    c: Coincident(g6,g-1)
    c: Horizontal(g0)
    c: DistanceY(g3,g0) = 90
FEATURE [PartDesign::Pocket] Pocket
  BaseFeature = -> Chamfer
  Direction = (0,0,1)
  Length = 3
  Length2 = 5
  Profile = -> Sketch006
  ReferenceAxis = -> Sketch006 [N_Axis]
  Refine = true
  Type = 0
FEATURE [Sketcher::SketchObject] Sketch007
  FullyConstrained = true
  MapMode = 5
  Placement = pos=(0,0,3) rot=(1,0,0;3.14159rad)
  Support = -> [Pocket]
  sketch-geometry (6):
    g0: Circle CenterX=-6.25 CenterY=-37.5 CenterZ=0 NormalX=0 NormalY=0 NormalZ=1 AngleXU=0 Radius=3.5
    g1: Circle CenterX=6.25 CenterY=-37.5 CenterZ=0 NormalX=0 NormalY=0 NormalZ=1 AngleXU=0 Radius=3.5
    g2: Circle CenterX=-6.25 CenterY=-25 CenterZ=0 NormalX=0 NormalY=0 NormalZ=1 AngleXU=0 Radius=3.5
    g3: Circle CenterX=6.25 CenterY=-25 CenterZ=0 NormalX=0 NormalY=0 NormalZ=1 AngleXU=0 Radius=3.5
    g4: Circle CenterX=6.25 CenterY=-12.5 CenterZ=0 NormalX=0 NormalY=0 NormalZ=1 AngleXU=0 Radius=3.5
    g5: Circle CenterX=-6.25 CenterY=-12.5 CenterZ=0 NormalX=0 NormalY=0 NormalZ=1 AngleXU=0 Radius=3.5
  constraints (15):
    c: Symmetric(g0,g1,g-2)
    c: Symmetric(g2,g3,g-2)
    c: DistanceX(g2,g3) = 12.5
    c: DistanceY(g1,g3) = 12.5
    c: Diameter(g3) = 7
    c: Equal(g2,g3)
    c: Equal(g0,g1)
    c: DistanceY(g3,g-1) = 25
    c: Vertical(g3,g1)
    c: Equal(g0,g2)
    c: Symmetric(g5,g4,g-2)
    c: Vertical(g2,g5)
    c: DistanceY(g3,g4) = 12.5
    c: Equal(g5,g2)
    c: Equal(g4,g5)
FEATURE [PartDesign::Pocket] Pocket001
  BaseFeature = -> Pocket
  Direction = (0,0,1)
  Length = 5
  Length2 = 5
  Profile = -> Sketch007
  ReferenceAxis = -> Sketch007 [N_Axis]
  Refine = true
  Type = 1
FEATURE [PartDesign::PolarPattern] PolarPattern002
  Angle = 360
  Axis = -> Z_Axis003
  BaseFeature = -> Pocket001
  Mode = 0
  Occurrences = 3
  Offset = 120
  Originals = -> [Pocket001]
  Refine = true
FEATURE [PartDesign::Chamfer] Chamfer001
  Angle = 45
  Base = -> PolarPattern002 [Edge68,Edge120,Edge121]
  BaseFeature = -> PolarPattern002
  ChamferType = 0
  FlipDirection = false
  Refine = true
  Size = 1
  Size2 = 1
  SupportTransform = false
  UseAllEdges = false
FEATURE [PartDesign::Body] Body002  label="plate-0"
  Group = -> [Sketch005,Pad002,Sketch004,Revolution001,PolarPattern001,Chamfer,Sketch006,Pocket,Sketch007,Pocket001,PolarPattern002,Chamfer001]
  Origin = -> Origin003
  Tip = -> Chamfer001
FEATURE [App::Part] Part  label="plate"
  Group = -> [Body001,Body002]
  Origin = -> Origin001
PROVENANCE & LICENSES
A FreeCAD (.FCStd) document from a public repository crawl; recipes are the document's own serialized feature recipes (and, for linked parts, companion documents' recipes).
License: lgpl-3.0.
